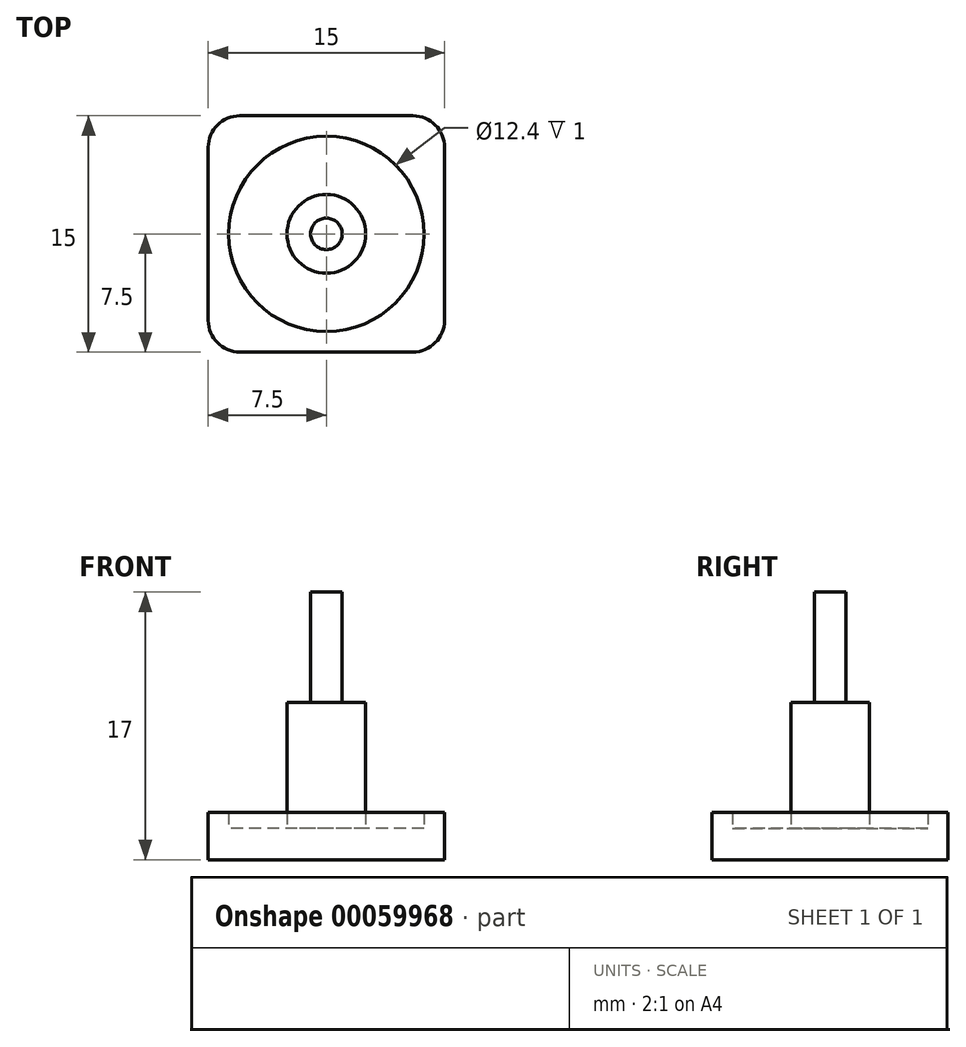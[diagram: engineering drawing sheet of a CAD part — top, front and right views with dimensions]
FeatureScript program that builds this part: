
annotation { "Feature Type Name" : "Feature", "Feature Type Description" : "" }
export const myFeature = defineFeature(function(context is Context, id is Id, definition is map)
    precondition{}
    {
        {
            var Q0;
            Q0=qCreatedBy(makeId("Top.planeOp"),FACE);
            var sketch = newSketch(context, id + "F0", { "sketchPlane" : qUnion([Q0])});
            skCircle(sketch, "E0", {"center": v(0, 0) * mm, "radius": 2.5 * mm});
            skSolve(sketch);
        }
        {
            var Q0;
            Q0=makeQuery(id+"F0.imprint","IMPRINT",FACE,{"disambiguationData":[TD([[makeQuery(id+"F0.imprint","IMPRINT",EDGE,{"derivedFrom":sQuery(id+"F0.wireOp",EDGE,"E0")}),1.0]])]});
            extrude(context, id + "F1", {"entities" : qUnion([Q0]), "depth" : 8 * mm});
        }
        {
            var Q0;
            Q0=makeQuery(id+"F1.opExtrude","CAP_FACE",FACE,{"disambiguationData":[OSD([sQuery(id+"F0.wireOp",EDGE,"E0")])],"isStart":false});
            var sketch = newSketch(context, id + "F2", { "sketchPlane" : qUnion([Q0])});
            skCircle(sketch, "E1", {"center": v(0, 0) * mm, "radius": 1 * mm});
            skSolve(sketch);
        }
        {
            var Q0;
            Q0=makeQuery(id+"F2.imprint","IMPRINT",FACE,{"disambiguationData":[TD([[makeQuery(id+"F2.imprint","IMPRINT",EDGE,{"derivedFrom":sQuery(id+"F2.wireOp",EDGE,"E1")}),1.0]])]});
            extrude(context, id + "F3", {"entities" : qUnion([Q0]), "operationType" : NewBodyOperationType.ADD, "depth" : 7 * mm});
        }
        {
            var Q0;
            Q0=makeQuery(id+"F1.opExtrude","CAP_FACE",FACE,{"disambiguationData":[OSD([sQuery(id+"F0.wireOp",EDGE,"E0")])],"isStart":true});
            var sketch = newSketch(context, id + "F4", { "sketchPlane" : qUnion([Q0])});
            skLineSegment(sketch, "E2.bottom", {"start": v(-5.5, 7.5) * mm, "end": v(5.5, 7.5) * mm});
            skLineSegment(sketch, "E2.top", {"start": v(-5.5, -7.5) * mm, "end": v(5.5, -7.5) * mm});
            skLineSegment(sketch, "E2.left", {"start": v(-7.5, 5.5) * mm, "end": v(-7.5, -5.5) * mm});
            skLineSegment(sketch, "E2.right", {"start": v(7.5, 5.5) * mm, "end": v(7.5, -5.5) * mm});
            skPoint(sketch, "E3.visualSharp", {"position": v(-7.5, 7.5) * mm});
            skArc(sketch, "E3.filletArc", {"start": v(-5.5, 7.5) * mm, "mid": v(-6.91, 6.91) * mm, "end": v(-7.5, 5.5) * mm});
            skPoint(sketch, "E4.visualSharp", {"position": v(7.5, 7.5) * mm});
            skArc(sketch, "E4.filletArc", {"start": v(7.5, 5.5) * mm, "mid": v(6.91, 6.91) * mm, "end": v(5.5, 7.5) * mm});
            skPoint(sketch, "E5.visualSharp", {"position": v(7.5, -7.5) * mm});
            skArc(sketch, "E5.filletArc", {"start": v(5.5, -7.5) * mm, "mid": v(6.91, -6.91) * mm, "end": v(7.5, -5.5) * mm});
            skPoint(sketch, "E6.visualSharp", {"position": v(-7.5, -7.5) * mm});
            skArc(sketch, "E6.filletArc", {"start": v(-7.5, -5.5) * mm, "mid": v(-6.91, -6.91) * mm, "end": v(-5.5, -7.5) * mm});
            skSolve(sketch);
        }
        {
            var Q0;
            Q0=makeQuery(id+"F4.imprint","IMPRINT",FACE,{"disambiguationData":[TD([[makeQuery(id+"F4.imprint","IMPRINT",EDGE,{"derivedFrom":sQuery(id+"F4.wireOp",EDGE,"E2.bottom")}),-1.0]])]});
            var Q1;
            Q1=makeQuery(id+"F4.imprint","IMPRINT",FACE,{"disambiguationData":[TD([[makeQuery(id+"F4.imprint","IMPRINT",EDGE,{"derivedFrom":makeQuery(id+"F1.opExtrude","CAP_EDGE",EDGE,{"disambiguationData":[OSD([sQuery(id+"F0.wireOp",EDGE,"E0")])],"isStart":true})}),-1.0]])]});
            extrude(context, id + "F5", {"entities" : qUnion([Q0, Q1]), "operationType" : NewBodyOperationType.ADD, "depth" : 2 * mm});
        }
        {
            var Q0;
            Q0=makeQuery(id+"F5.opExtrude","CAP_FACE",FACE,{"disambiguationData":[OSD([sQuery(id+"F4.wireOp",EDGE,"E2.bottom"),sQuery(id+"F4.wireOp",EDGE,"E2.top"),sQuery(id+"F4.wireOp",EDGE,"E2.left"),sQuery(id+"F4.wireOp",EDGE,"E2.right"),sQuery(id+"F4.wireOp",EDGE,"E3.filletArc"),sQuery(id+"F4.wireOp",EDGE,"E4.filletArc"),sQuery(id+"F4.wireOp",EDGE,"E5.filletArc"),sQuery(id+"F4.wireOp",EDGE,"E6.filletArc")])],"isStart":true});
            var sketch = newSketch(context, id + "F6", { "sketchPlane" : qUnion([Q0])});
            skCircle(sketch, "E7", {"center": v(0, 0) * mm, "radius": 6.2 * mm});
            skLineSegment(sketch, "E8.0", {"start": v(-5.5, 7.5) * mm, "end": v(5.5, 7.5) * mm});
            skArc(sketch, "E8.1", {"start": v(-7.5, 5.5) * mm, "mid": v(-6.91, 6.91) * mm, "end": v(-5.5, 7.5) * mm});
            skLineSegment(sketch, "E8.2", {"start": v(-7.5, -5.5) * mm, "end": v(-7.5, 5.5) * mm});
            skArc(sketch, "E8.3", {"start": v(-5.5, -7.5) * mm, "mid": v(-6.91, -6.91) * mm, "end": v(-7.5, -5.5) * mm});
            skLineSegment(sketch, "E8.4", {"start": v(-5.5, -7.5) * mm, "end": v(5.5, -7.5) * mm});
            skArc(sketch, "E8.5", {"start": v(7.5, -5.5) * mm, "mid": v(6.91, -6.91) * mm, "end": v(5.5, -7.5) * mm});
            skLineSegment(sketch, "E8.6", {"start": v(7.5, -5.5) * mm, "end": v(7.5, 5.5) * mm});
            skArc(sketch, "E8.7", {"start": v(5.5, 7.5) * mm, "mid": v(6.91, 6.91) * mm, "end": v(7.5, 5.5) * mm});
            skSolve(sketch);
        }
        {
            var Q0;
            Q0 = qSketchRegion(id + "F6", true);
            var Q1;
            Q1=makeQuery(id+"F6.imprint","IMPRINT",FACE,{"disambiguationData":[TD([[makeQuery(id+"F6.imprint","IMPRINT",EDGE,{"derivedFrom":sQuery(id+"F6.wireOp",EDGE,"E7")}),-1.0]])]});
            extrude(context, id + "F7", {"entities" : qUnion([Q0, Q1]), "operationType" : NewBodyOperationType.ADD, "depth" : 1 * mm});
        }
    });
